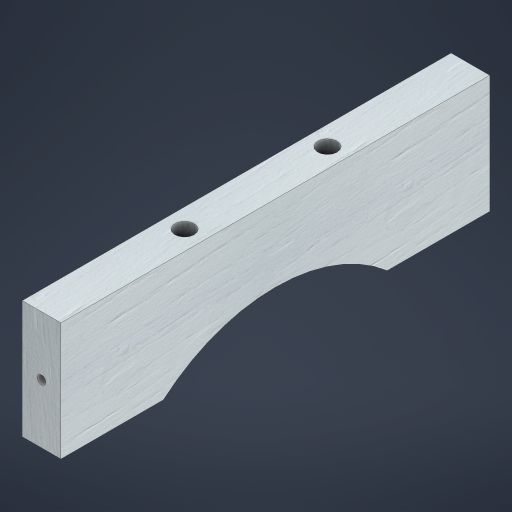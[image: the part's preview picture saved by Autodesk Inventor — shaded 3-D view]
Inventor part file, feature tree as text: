
AUTODESK INVENTOR PART (.ipt)
format: ipt  version: 2024 (Build 280153000, 153)  size: 339,456 bytes
history: native  units: mm
features: extrude x4, sketch x2, other x1
ambient origin geometry x8: Origin, YZ Plane, XZ Plane, XY Plane, X Axis, Y Axis, Z Axis, Center Point
bodies: Body1 (feature_tree)
feature tree (7):
  other  "Sólido1"
  extrude  "Extrusión1"  Depth=9.0mm
  extrude  "Extrusión2"  Depth=18.0mm
  extrude  "Extrusión3"  Depth=18.0mm
  extrude  "Extrusión4"  Depth=18.0mm
  sketch  "Boceto3"  dims[d3=0.0mm d4=9.0mm]
  sketch  "Boceto4"  dims[d5=9.0mm d7=66.666667mm d8=9.0mm d9=9.0mm d10=6.0mm d11=0.0mm d14=100.0mm d15=18.0mm d16=0.0mm d17=4.0mm d18=27.5mm d19=290.0mm d20=0.0mm]
